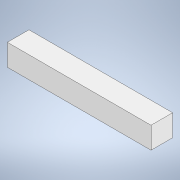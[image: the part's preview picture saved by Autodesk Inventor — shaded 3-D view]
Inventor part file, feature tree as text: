
AUTODESK INVENTOR PART (.ipt)
format: ipt  version: 2021 (Build 250183000, 183)  size: 91,136 bytes
history: native  units: in
note: dims shown in document units (in); Inventor stores cm internally (conversion verified against a paired STEP export)
features: extrude x1
ambient origin geometry x8: Origin, YZ Plane, XZ Plane, XY Plane, X Axis, Y Axis, Z Axis, Center Point
bodies: Solid1 (feature_tree)
feature tree (1):
  extrude  "Extrusion1"  Depth=5.8125in
